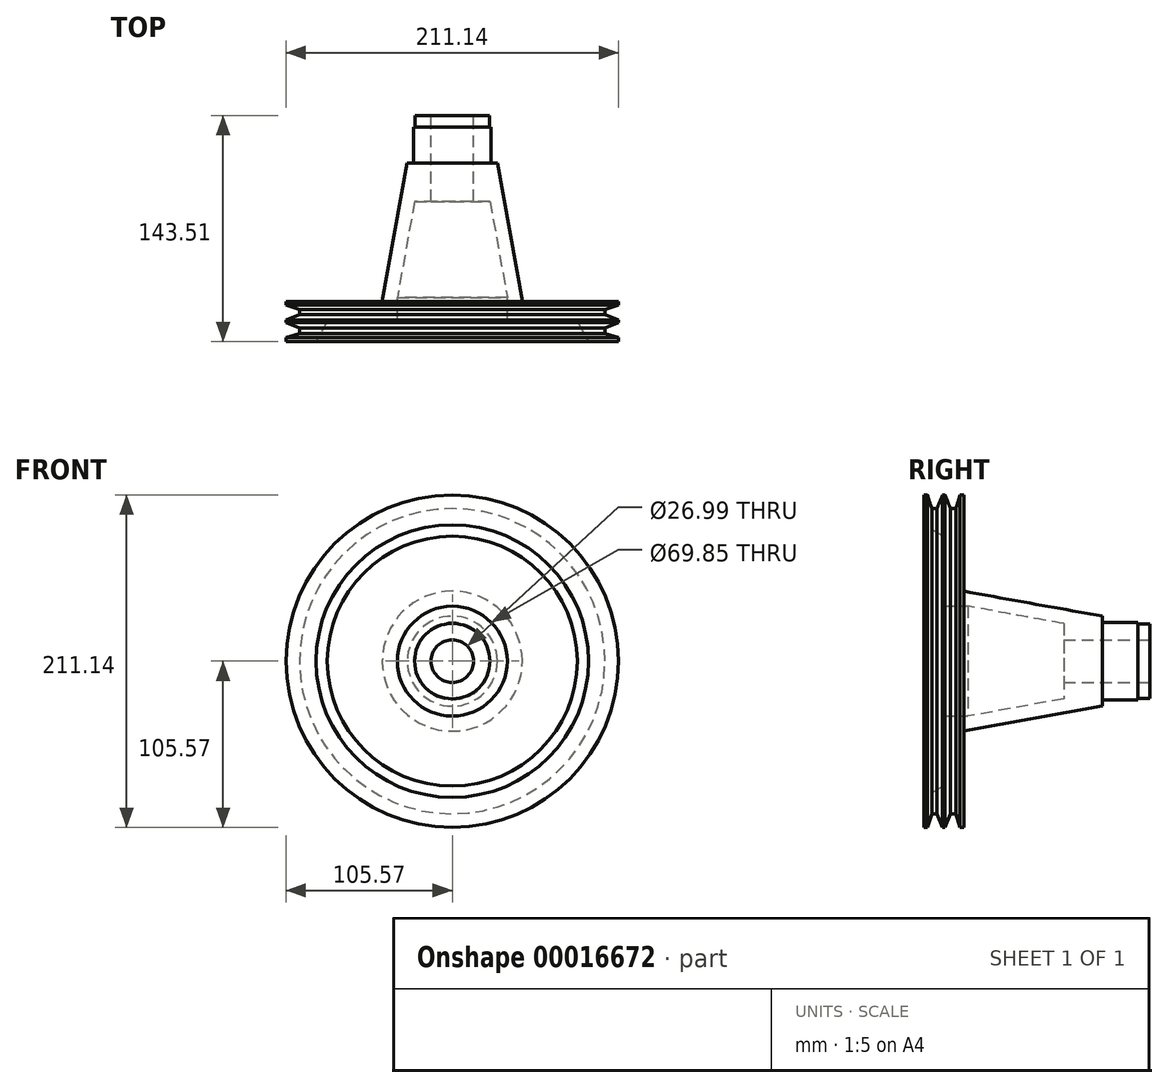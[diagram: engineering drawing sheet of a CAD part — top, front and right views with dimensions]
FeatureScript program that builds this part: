
annotation { "Feature Type Name" : "Feature", "Feature Type Description" : "" }
export const myFeature = defineFeature(function(context is Context, id is Id, definition is map)
    precondition{}
    {
        {
            var Q0;
            Q0=qCreatedBy(makeId("Right.planeOp"),FACE);
            var sketch = newSketch(context, id + "F0", { "sketchPlane" : qUnion([Q0])});
            skLineSegment(sketch, "E0", {"start": v(90.65, 0) * mm, "end": v(-135.16, 0) * mm, "construction": true});
            skLineSegment(sketch, "E1", {"start": v(0, 13.5) * mm, "end": v(0, 23.79) * mm});
            skLineSegment(sketch, "E2", {"start": v(0, 23.79) * mm, "end": v(-7.47, 23.79) * mm});
            skLineSegment(sketch, "E3", {"start": v(-7.47, 23.79) * mm, "end": v(-7.47, 24.57) * mm});
            skLineSegment(sketch, "E4", {"start": v(-7.47, 24.57) * mm, "end": v(-30.05, 24.57) * mm});
            skLineSegment(sketch, "E5", {"start": v(-30.05, 24.57) * mm, "end": v(-30.05, 28.57) * mm});
            skLineSegment(sketch, "E6", {"start": v(-30.05, 28.57) * mm, "end": v(-118.11, 44.45) * mm});
            skLineSegment(sketch, "E7", {"start": v(-118.11, 44.45) * mm, "end": v(-118.11, 105.57) * mm});
            skLineSegment(sketch, "E8", {"start": v(-118.11, 105.57) * mm, "end": v(-120.5, 105.57) * mm});
            skLineSegment(sketch, "E9", {"start": v(-120.5, 105.57) * mm, "end": v(-123.2, 96.93) * mm});
            skLineSegment(sketch, "E10", {"start": v(-123.2, 96.93) * mm, "end": v(-126.5, 96.93) * mm});
            skLineSegment(sketch, "E11", {"start": v(-126.5, 96.93) * mm, "end": v(-130.02, 105.57) * mm});
            skLineSegment(sketch, "E12", {"start": v(-130.02, 105.57) * mm, "end": v(-131.6, 105.57) * mm});
            skLineSegment(sketch, "E13", {"start": v(-131.6, 105.57) * mm, "end": v(-135.13, 96.93) * mm});
            skLineSegment(sketch, "E14", {"start": v(-135.13, 96.93) * mm, "end": v(-138.43, 96.93) * mm});
            skLineSegment(sketch, "E15", {"start": v(-138.43, 96.93) * mm, "end": v(-141.12, 105.57) * mm});
            skLineSegment(sketch, "E16", {"start": v(-141.12, 105.57) * mm, "end": v(-143.51, 105.57) * mm});
            skLineSegment(sketch, "E17", {"start": v(-143.51, 105.57) * mm, "end": v(-143.51, 86.52) * mm});
            skLineSegment(sketch, "E18", {"start": v(-143.51, 86.52) * mm, "end": v(-130.8, 79.37) * mm});
            skLineSegment(sketch, "E19", {"start": v(-130.8, 79.37) * mm, "end": v(-130.8, 34.92) * mm});
            skLineSegment(sketch, "E20", {"start": v(-130.8, 34.92) * mm, "end": v(-115.57, 34.92) * mm});
            skLineSegment(sketch, "E21", {"start": v(-115.57, 34.92) * mm, "end": v(-54.6, 23.94) * mm});
            skLineSegment(sketch, "E22", {"start": v(-54.6, 23.94) * mm, "end": v(-54.6, 13.5) * mm});
            skLineSegment(sketch, "E23", {"start": v(-54.6, 13.5) * mm, "end": v(0, 13.5) * mm});
            skSolve(sketch);
        }
        {
            var Q0;
            Q0=makeQuery(id+"F0.imprint","IMPRINT",FACE,{"disambiguationData":[TD([[makeQuery(id+"F0.imprint","IMPRINT",EDGE,{"derivedFrom":sQuery(id+"F0.wireOp",EDGE,"E1")}),1.0]])]});
            var Q1;
            Q1=sQuery(id+"F0.wireOp",EDGE,"E0");
            revolve(context, id + "F1", {"surfaceOperationType" : NewSurfaceOperationType.NEW, "entities" : qUnion([Q0]), "axis" : qUnion([Q1]), "revolveType" : RevolveType.FULL});
        }
    });
